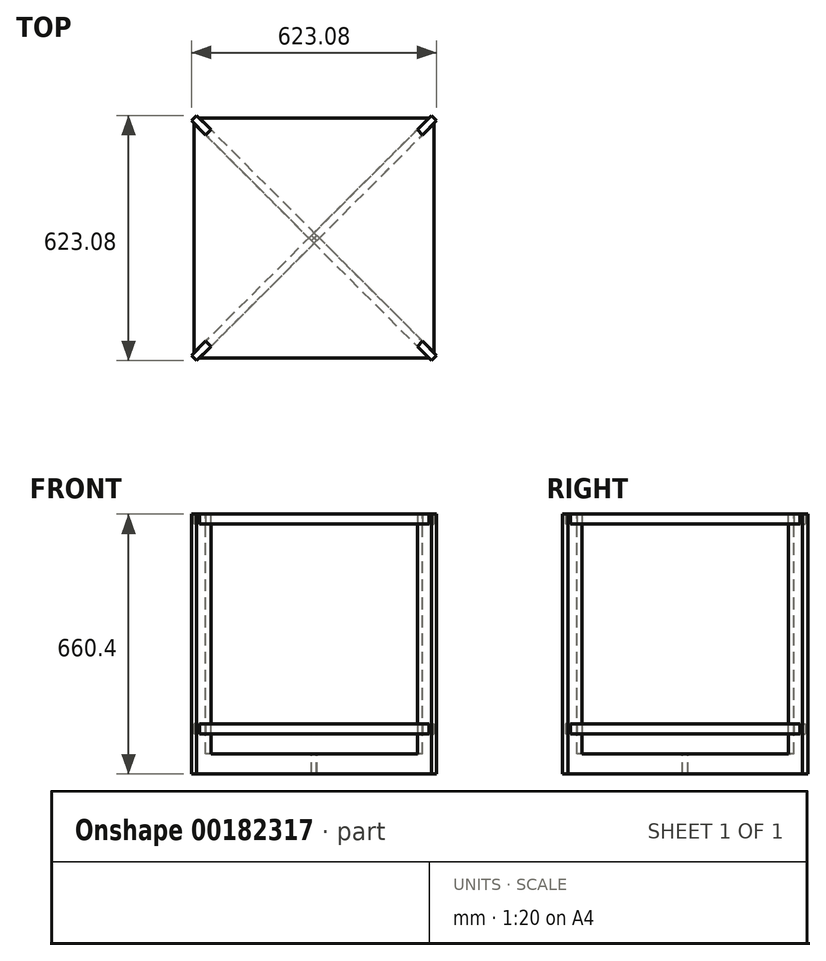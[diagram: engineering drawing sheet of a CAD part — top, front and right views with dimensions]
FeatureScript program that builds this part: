
annotation { "Feature Type Name" : "Feature", "Feature Type Description" : "" }
export const myFeature = defineFeature(function(context is Context, id is Id, definition is map)
    precondition{}
    {
        {
            var Q0;
            Q0=qCreatedBy(makeId("Top.planeOp"),FACE);
            var sketch = newSketch(context, id + "F0", { "sketchPlane" : qUnion([Q0])});
            skLineSegment(sketch, "E0.bottom", {"start": v(0, 0) * mm, "end": v(609.6, 0) * mm});
            skLineSegment(sketch, "E0.top", {"start": v(0, 609.6) * mm, "end": v(609.6, 609.6) * mm});
            skLineSegment(sketch, "E0.left", {"start": v(0, 0) * mm, "end": v(0, 609.6) * mm});
            skLineSegment(sketch, "E0.right", {"start": v(609.6, 0) * mm, "end": v(609.6, 609.6) * mm});
            skPoint(sketch, "E1", {"position": v(304.8, 304.8) * mm});
            skSolve(sketch);
        }
        {
            var Q0;
            Q0=qCreatedBy(makeId("Top.planeOp"),FACE);
            cPlane(context, id + "F1", {"entities" : qUnion([Q0]), "cplaneType" : CPlaneType.OFFSET, "offset" : 660.4 * mm, "width" : 152.4 * mm, "height" : 152.4 * mm});
        }
        {
            var Q0;
            Q0=qCreatedBy(id+"F1.planeOp",FACE);
            var sketch = newSketch(context, id + "F2", { "sketchPlane" : qUnion([Q0])});
            skLineSegment(sketch, "E2.bottom", {"start": v(0, 0) * mm, "end": v(609.6, 0) * mm});
            skLineSegment(sketch, "E2.top", {"start": v(0, 609.6) * mm, "end": v(609.6, 609.6) * mm});
            skLineSegment(sketch, "E2.left", {"start": v(0, 0) * mm, "end": v(0, 609.6) * mm});
            skLineSegment(sketch, "E2.right", {"start": v(609.6, 0) * mm, "end": v(609.6, 609.6) * mm});
            skLineSegment(sketch, "E3", {"start": v(-6.74, 602.86) * mm, "end": v(0, 609.6) * mm});
            skLineSegment(sketch, "E4", {"start": v(0, 609.6) * mm, "end": v(6.74, 616.34) * mm});
            skLineSegment(sketch, "E5", {"start": v(-6.74, 602.86) * mm, "end": v(29.19, 566.94) * mm});
            skLineSegment(sketch, "E6", {"start": v(29.19, 566.94) * mm, "end": v(42.66, 580.41) * mm});
            skLineSegment(sketch, "E7", {"start": v(42.66, 580.41) * mm, "end": v(6.74, 616.34) * mm});
            skPoint(sketch, "E8", {"position": v(304.8, 304.8) * mm});
            skSolve(sketch);
        }
        {
            var Q0;
            {var subQ6=sQuery(id+"F2.wireOp",EDGE,"E2.bottom");Q0=makeQuery(id+"F2.imprint","IMPRINT",FACE,{"disambiguationData":[TD([[makeQuery(id+"F2.imprint","IMPRINT",EDGE,{"derivedFrom":subQ6}),1.0]])]});}
            var sketch = newSketch(context, id + "F3", { "sketchPlane" : qUnion([Q0])});
            skPoint(sketch, "E9.0", {"position": v(3.37, 612.97) * mm});
            skLineSegment(sketch, "E10.0", {"start": v(0, 609.6) * mm, "end": v(6.74, 616.34) * mm});
            skLineSegment(sketch, "E11.0", {"start": v(-6.74, 602.86) * mm, "end": v(0, 609.6) * mm});
            skLineSegment(sketch, "E12.0", {"start": v(-6.74, 602.86) * mm, "end": v(29.19, 566.94) * mm});
            skLineSegment(sketch, "E13.0", {"start": v(29.19, 566.94) * mm, "end": v(42.66, 580.41) * mm});
            skLineSegment(sketch, "E14.0", {"start": v(42.66, 580.41) * mm, "end": v(6.74, 616.34) * mm});
            skSolve(sketch);
        }
        {
            var Q0;
            Q0 = qSketchRegion(id + "F3", true);
            extrude(context, id + "F4", {"entities" : qUnion([Q0]), "oppositeDirection" : true, "depth" : 660.4 * mm});
        }
        {
            var Q0;
            Q0=makeQuery(id+"F4.opExtrude","SWEPT_FACE",FACE,{"disambiguationData":[OSD([sQuery(id+"F3.wireOp",EDGE,"E13.0")])]});
            var sketch = newSketch(context, id + "F5", { "sketchPlane" : qUnion([Q0])});
            skLineSegment(sketch, "E15.bottom", {"start": v(440.58, 0) * mm, "end": v(421.53, 0) * mm});
            skLineSegment(sketch, "E15.top", {"start": v(440.58, 50.8) * mm, "end": v(421.53, 50.8) * mm});
            skLineSegment(sketch, "E15.left", {"start": v(440.58, 0) * mm, "end": v(440.58, 50.8) * mm});
            skLineSegment(sketch, "E15.right", {"start": v(421.53, 0) * mm, "end": v(421.53, 50.8) * mm});
            skSolve(sketch);
        }
        {
            var Q0;
            Q0=makeQuery(id+"F5.imprint","IMPRINT",FACE,{"disambiguationData":[TD([[makeQuery(id+"F5.imprint","IMPRINT",EDGE,{"derivedFrom":sQuery(id+"F5.wireOp",EDGE,"E15.bottom")}),1.0]])]});
            extrude(context, id + "F6", {"entities" : qUnion([Q0]), "operationType" : NewBodyOperationType.ADD, "depth" : 380.24 * mm});
        }
        {
            var Q0;
            Q0=qCreatedBy(makeId("Right.planeOp"),FACE);
            cPlane(context, id + "F7", {"entities" : qUnion([Q0]), "cplaneType" : CPlaneType.OFFSET, "offset" : 304.8 * mm, "width" : 152.4 * mm, "height" : 152.4 * mm});
        }
        {
            var Q0;
            Q0=qCreatedBy(id+"F7.planeOp",FACE);
            var sketch = newSketch(context, id + "F8", { "sketchPlane" : qUnion([Q0])});
            skLineSegment(sketch, "E16", {"start": v(304.8, 1072.96) * mm, "end": v(304.8, -266.55) * mm});
            skSolve(sketch);
        }
        {
            var Q0;
            Q0=makeQuery(id+"F4.opExtrude","SWEPT_BODY",BODY,{"disambiguationData":[OSD([sQuery(id+"F3.wireOp",EDGE,"E10.0"),sQuery(id+"F3.wireOp",EDGE,"E11.0"),sQuery(id+"F3.wireOp",EDGE,"E12.0"),sQuery(id+"F3.wireOp",EDGE,"E13.0"),sQuery(id+"F3.wireOp",EDGE,"E14.0")])]});
            var Q1;
            Q1=sQuery(id+"F8.wireOp",EDGE,"E16");
            circularPattern(context, id + "F9", {"entities" : qUnion([Q0]), "axis" : qUnion([Q1]), "angle" : 90 * degree, "instanceCount" : 4});
        }
        {
            var Q0;
            Q0=qCreatedBy(makeId("Top.planeOp"),FACE);
            cPlane(context, id + "F10", {"entities" : qUnion([Q0]), "cplaneType" : CPlaneType.OFFSET, "offset" : 101.6 * mm, "width" : 152.4 * mm, "height" : 152.4 * mm});
        }
        {
            var Q0;
            Q0=qCreatedBy(id+"F10.planeOp",FACE);
            var sketch = newSketch(context, id + "F11", { "sketchPlane" : qUnion([Q0])});
            skLineSegment(sketch, "E17.bottom", {"start": v(13.47, 0) * mm, "end": v(596.13, 0) * mm});
            skLineSegment(sketch, "E17.top", {"start": v(13.47, 609.6) * mm, "end": v(596.13, 609.6) * mm});
            skLineSegment(sketch, "E17.left", {"start": v(0, 13.47) * mm, "end": v(0, 596.13) * mm});
            skLineSegment(sketch, "E17.right", {"start": v(609.6, 13.47) * mm, "end": v(609.6, 596.13) * mm});
            skLineSegment(sketch, "E18", {"start": v(42.66, 580.41) * mm, "end": v(29.19, 566.94) * mm});
            skLineSegment(sketch, "E19", {"start": v(42.66, 580.41) * mm, "end": v(13.47, 609.6) * mm});
            skLineSegment(sketch, "E20", {"start": v(29.19, 566.94) * mm, "end": v(0, 596.13) * mm});
            skLineSegment(sketch, "E21", {"start": v(566.94, 580.41) * mm, "end": v(580.41, 566.94) * mm});
            skLineSegment(sketch, "E22", {"start": v(566.94, 580.41) * mm, "end": v(596.13, 609.6) * mm});
            skLineSegment(sketch, "E23", {"start": v(580.41, 566.94) * mm, "end": v(609.6, 596.13) * mm});
            skLineSegment(sketch, "E24", {"start": v(566.94, 29.19) * mm, "end": v(580.41, 42.66) * mm});
            skLineSegment(sketch, "E25", {"start": v(580.41, 42.66) * mm, "end": v(609.6, 13.47) * mm});
            skLineSegment(sketch, "E26", {"start": v(566.94, 29.19) * mm, "end": v(596.13, 0) * mm});
            skLineSegment(sketch, "E27", {"start": v(29.19, 42.66) * mm, "end": v(42.66, 29.19) * mm});
            skLineSegment(sketch, "E28", {"start": v(29.19, 42.66) * mm, "end": v(0, 13.47) * mm});
            skLineSegment(sketch, "E29", {"start": v(42.66, 29.19) * mm, "end": v(13.47, 0) * mm});
            skPoint(sketch, "E30.orphan", {"position": v(0, 0) * mm});
            skSolve(sketch);
        }
        {
            var Q0;
            Q0=makeQuery(id+"F11.imprint","IMPRINT",FACE,{"disambiguationData":[TD([[makeQuery(id+"F11.imprint","IMPRINT",EDGE,{"derivedFrom":sQuery(id+"F11.wireOp",EDGE,"E17.bottom")}),1.0]])]});
            extrude(context, id + "F12", {"entities" : qUnion([Q0]), "depth" : 25.4 * mm});
        }
        {
            var Q0;
            Q0=makeQuery(id+"F12.opExtrude","SWEPT_BODY",BODY,{"disambiguationData":[OSD([sQuery(id+"F11.wireOp",EDGE,"E17.bottom"),sQuery(id+"F11.wireOp",EDGE,"E17.top"),sQuery(id+"F11.wireOp",EDGE,"E17.left"),sQuery(id+"F11.wireOp",EDGE,"E17.right"),sQuery(id+"F11.wireOp",EDGE,"E18"),sQuery(id+"F11.wireOp",EDGE,"E19"),sQuery(id+"F11.wireOp",EDGE,"E20"),sQuery(id+"F11.wireOp",EDGE,"E21"),sQuery(id+"F11.wireOp",EDGE,"E22"),sQuery(id+"F11.wireOp",EDGE,"E23"),sQuery(id+"F11.wireOp",EDGE,"E24"),sQuery(id+"F11.wireOp",EDGE,"E25"),sQuery(id+"F11.wireOp",EDGE,"E26"),sQuery(id+"F11.wireOp",EDGE,"E27"),sQuery(id+"F11.wireOp",EDGE,"E28"),sQuery(id+"F11.wireOp",EDGE,"E29")])]});
            transform(context, id + "F13", {"entities" : qUnion([Q0]), "transformType" : TransformType.TRANSLATION_3D, "dx" : 0 * mm, "dy" : 0 * mm, "dz" : 533.4 * mm, "makeCopy" : true});
        }
    });
